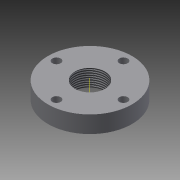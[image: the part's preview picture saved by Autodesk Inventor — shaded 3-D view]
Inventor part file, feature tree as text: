
AUTODESK INVENTOR PART (.ipt)
format: ipt  version: 2013 (Build 170138000, 138)  size: 92,672 bytes
history: native  units: in
note: dims shown in document units (in); Inventor stores cm internally (conversion verified against a paired STEP export)
features: extrude x1, thread x1, other x1, sketch x1
ambient origin geometry x8: Origin, YZ Plane, XZ Plane, XY Plane, X Axis, Y Axis, Z Axis, Center Point
bodies: Solid1 (feature_tree)
feature tree (4):
  extrude  "Extrusion1"  Depth=2.09in
  thread  "Thread1"  [1 undecoded]
  other  "Work Axis1"
  sketch  "Sketch1"  dims[d0=2.62in d1=2.09in d2=0.26in d3=0.26in d4=0.26in d5=0.26in d6=0.937in d7=0.53in d8=0.0in d9=1.0in d10=0.0in]
note: 1 required parameter value undecoded (feature->parameter linkage not recoverable at this tier; creation-order binding heuristic only, values carry confidence <= 0.55)
